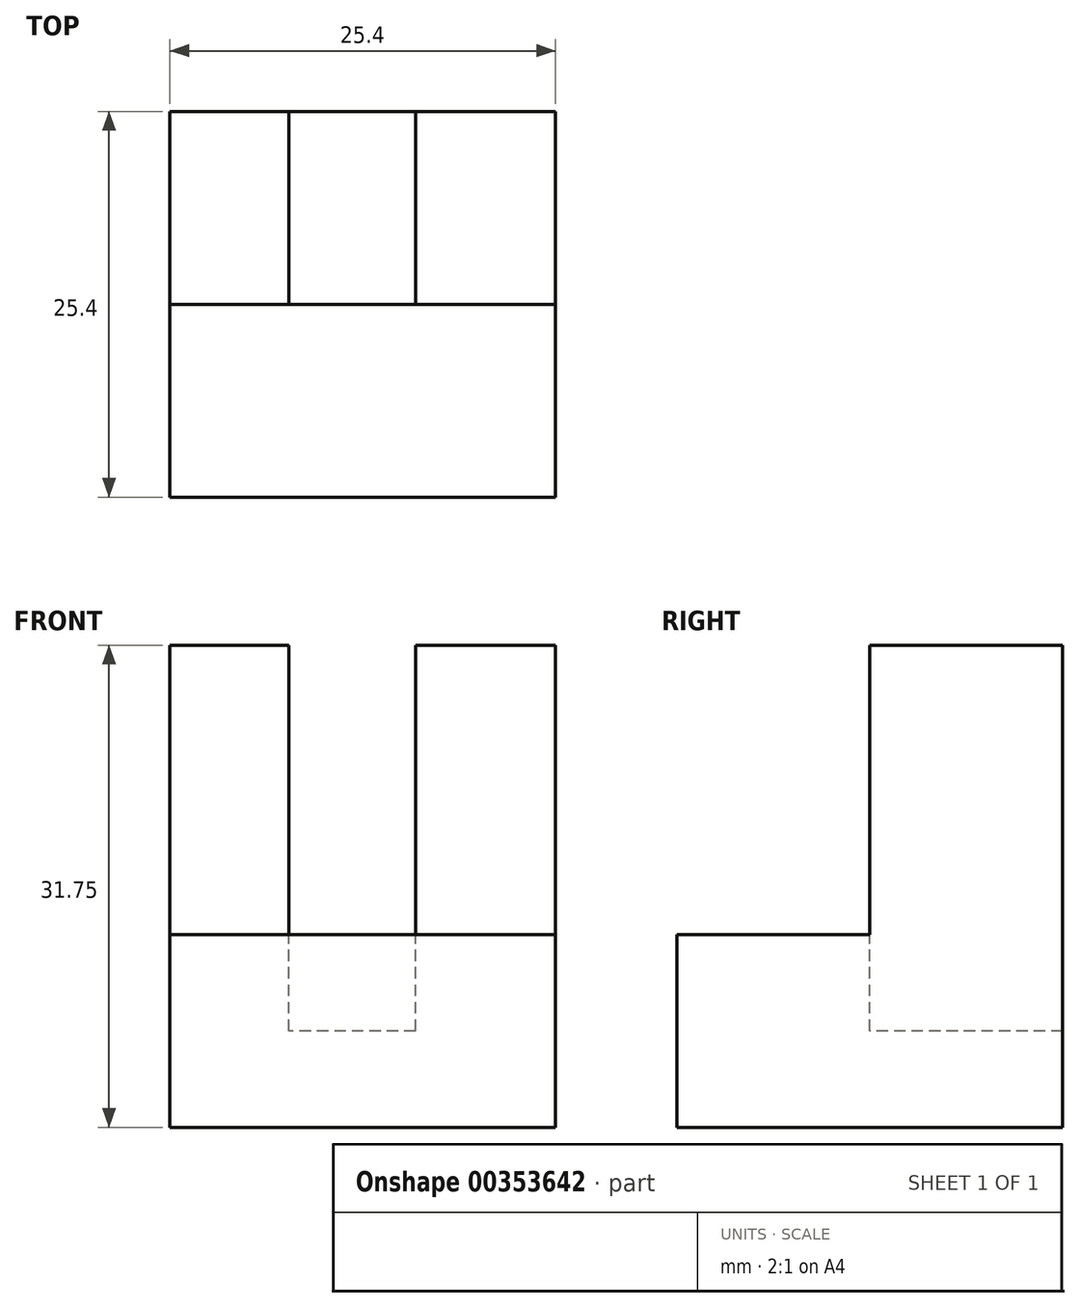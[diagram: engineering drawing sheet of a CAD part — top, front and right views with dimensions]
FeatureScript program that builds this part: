
annotation { "Feature Type Name" : "Feature", "Feature Type Description" : "" }
export const myFeature = defineFeature(function(context is Context, id is Id, definition is map)
    precondition{}
    {
        {
            var Q0;
            Q0=qCreatedBy(makeId("Right.planeOp"),FACE);
            var sketch = newSketch(context, id + "F0", { "sketchPlane" : qUnion([Q0])});
            skLineSegment(sketch, "E0", {"start": v(-32.36, 12.7) * mm, "end": v(-32.36, 0) * mm});
            skLineSegment(sketch, "E1", {"start": v(-32.36, 12.7) * mm, "end": v(-19.66, 12.7) * mm});
            skLineSegment(sketch, "E2", {"start": v(-19.66, 12.7) * mm, "end": v(-19.66, 31.75) * mm});
            skLineSegment(sketch, "E3", {"start": v(-19.66, 31.75) * mm, "end": v(-6.96, 31.75) * mm});
            skLineSegment(sketch, "E4", {"start": v(-6.96, 31.75) * mm, "end": v(-6.96, 0) * mm});
            skLineSegment(sketch, "E5", {"start": v(-32.36, 0) * mm, "end": v(-6.96, 0) * mm});
            skSolve(sketch);
        }
        {
            var Q0;
            Q0 = qSketchRegion(id + "F0", true);
            extrude(context, id + "F1", {"entities" : qUnion([Q0]), "depth" : 25.4 * mm});
        }
        {
            var Q0;
            Q0=makeQuery(id+"F1.opExtrude","SWEPT_FACE",FACE,{"disambiguationData":[OSD([sQuery(id+"F0.wireOp",EDGE,"E3")])]});
            var sketch = newSketch(context, id + "F2", { "sketchPlane" : qUnion([Q0])});
            skLineSegment(sketch, "E6", {"start": v(7.83, -6.96) * mm, "end": v(7.83, -19.66) * mm});
            skLineSegment(sketch, "E7", {"start": v(16.18, -6.96) * mm, "end": v(16.18, -19.66) * mm});
            skPoint(sketch, "E7.endSnap0", {"position": v(12.7, -19.66) * mm});
            skLineSegment(sketch, "E8", {"start": v(16.18, -19.66) * mm, "end": v(7.83, -19.66) * mm});
            skLineSegment(sketch, "E9", {"start": v(7.83, -6.96) * mm, "end": v(16.18, -6.96) * mm});
            skSolve(sketch);
        }
        {
            var Q0;
            Q0 = qSketchRegion(id + "F2", true);
            extrude(context, id + "F3", {"entities" : qUnion([Q0]), "operationType" : NewBodyOperationType.REMOVE, "oppositeDirection" : true, "depth" : 25.4 * mm});
        }
    });
